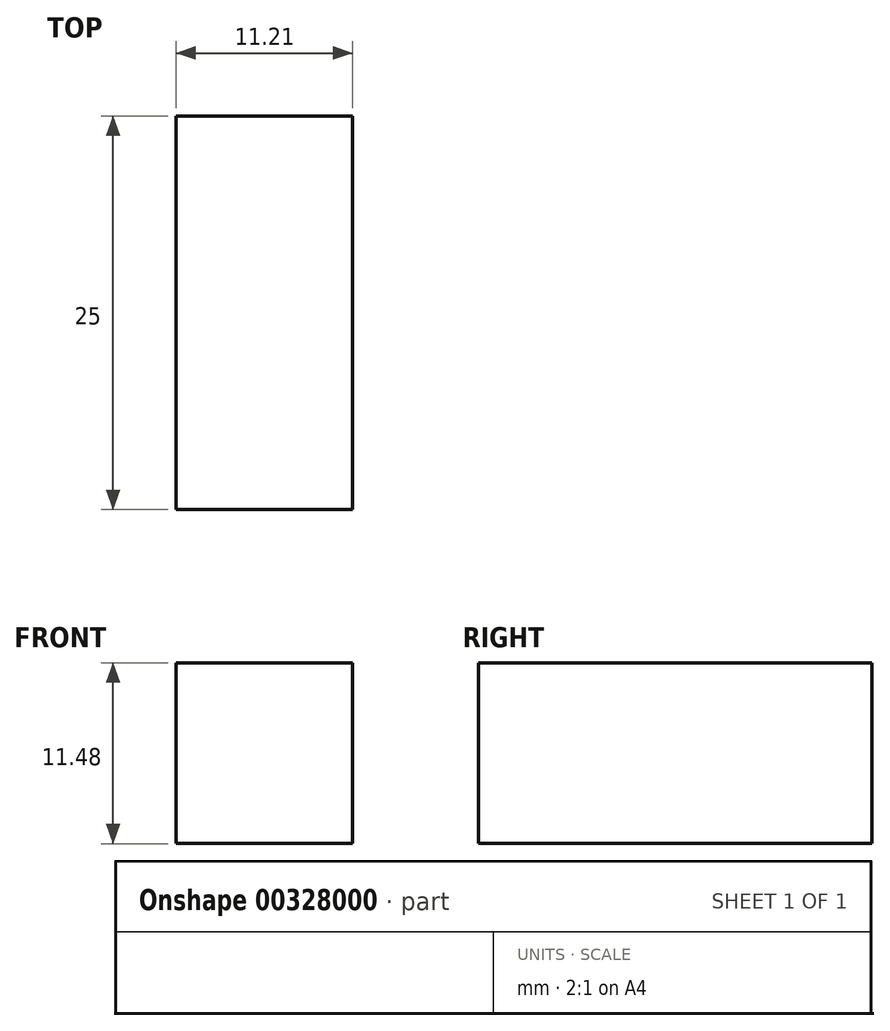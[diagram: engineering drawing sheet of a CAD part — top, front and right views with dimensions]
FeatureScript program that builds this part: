
annotation { "Feature Type Name" : "Feature", "Feature Type Description" : "" }
export const myFeature = defineFeature(function(context is Context, id is Id, definition is map)
    precondition{}
    {
        {
            var Q0;
            Q0=qCreatedBy(makeId("Front.planeOp"),FACE);
            var sketch = newSketch(context, id + "F0", { "sketchPlane" : qUnion([Q0])});
            skLineSegment(sketch, "E0", {"start": v(-37.41, 34.57) * mm, "end": v(37.2, 34.57) * mm});
            skLineSegment(sketch, "E1.bottom", {"start": v(-51.1, 19.3) * mm, "end": v(-39.9, 19.3) * mm});
            skLineSegment(sketch, "E1.top", {"start": v(-51.1, 7.82) * mm, "end": v(-39.9, 7.82) * mm});
            skLineSegment(sketch, "E1.left", {"start": v(-51.1, 19.3) * mm, "end": v(-51.1, 7.82) * mm});
            skLineSegment(sketch, "E1.right", {"start": v(-39.9, 19.3) * mm, "end": v(-39.9, 7.82) * mm});
            skSolve(sketch);
        }
        {
            var Q0;
            Q0 = qSketchRegion(id + "F0", true);
            extrude(context, id + "F1", {"entities" : qUnion([Q0]), "depth" : 30.8 * mm});
        }
        {
            var Q0;
            Q0=makeQuery(id+"F0.imprint","IMPRINT",FACE,{"disambiguationData":[TD([[makeQuery(id+"F0.imprint","IMPRINT",EDGE,{"derivedFrom":sQuery(id+"F0.wireOp",EDGE,"E1.bottom")}),-1.0]])]});
            extrude(context, id + "F2", {"entities" : qUnion([Q0]), "operationType" : NewBodyOperationType.INTERSECT, "depth" : 25 * mm});
        }
    });
